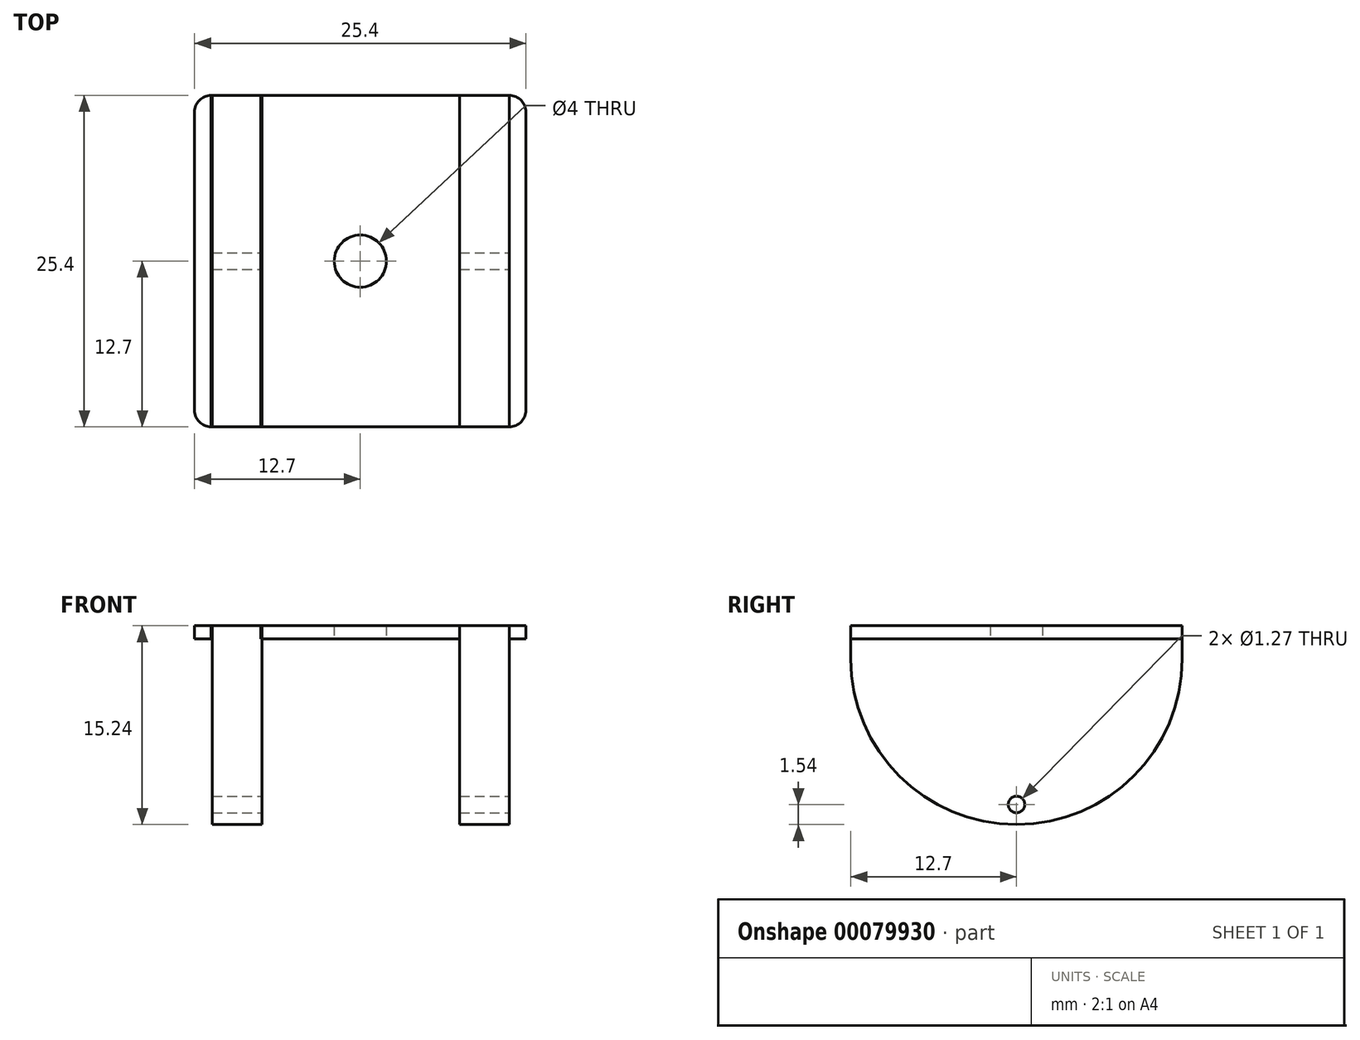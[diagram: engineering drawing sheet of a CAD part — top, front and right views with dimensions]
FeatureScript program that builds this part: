
annotation { "Feature Type Name" : "Feature", "Feature Type Description" : "" }
export const myFeature = defineFeature(function(context is Context, id is Id, definition is map)
    precondition{}
    {
        {
            var Q0;
            Q0=qCreatedBy(makeId("Top.planeOp"),FACE);
            var sketch = newSketch(context, id + "F0", { "sketchPlane" : qUnion([Q0])});
            skLineSegment(sketch, "E0.bottom", {"start": v(12.7, -12.7) * mm, "end": v(-12.7, -12.7) * mm});
            skLineSegment(sketch, "E0.top", {"start": v(12.7, 12.7) * mm, "end": v(-12.7, 12.7) * mm});
            skLineSegment(sketch, "E0.left", {"start": v(12.7, -12.7) * mm, "end": v(12.7, 12.7) * mm});
            skLineSegment(sketch, "E0.right", {"start": v(-12.7, -12.7) * mm, "end": v(-12.7, 12.7) * mm});
            skPoint(sketch, "E0.middle", {"position": v(0, 0) * mm});
            skLineSegment(sketch, "E1.bottom", {"start": v(-7.62, -12.7) * mm, "end": v(-11.43, -12.7) * mm});
            skLineSegment(sketch, "E1.top", {"start": v(-7.62, 12.7) * mm, "end": v(-11.43, 12.7) * mm});
            skLineSegment(sketch, "E1.left", {"start": v(-7.62, -12.7) * mm, "end": v(-7.62, 12.7) * mm});
            skLineSegment(sketch, "E1.right", {"start": v(-11.43, -12.7) * mm, "end": v(-11.43, 12.7) * mm});
            skPoint(sketch, "E1.middle", {"position": v(-9.53, 0) * mm});
            skPoint(sketch, "E1.middle.positionSnap0", {"position": v(-12.7, 0) * mm});
            skPoint(sketch, "E1.centerSnap0", {"position": v(-12.7, 0) * mm});
            skLineSegment(sketch, "E2", {"start": v(0, 12.7) * mm, "end": v(0, -12.7) * mm});
            skLineSegment(sketch, "E3.MirrorCS", {"start": v(11.43, -12.7) * mm, "end": v(11.43, 12.7) * mm});
            skLineSegment(sketch, "E4.MirrorCS", {"start": v(7.62, -12.7) * mm, "end": v(7.62, 12.7) * mm});
            skCircle(sketch, "E5", {"center": v(0, 0) * mm, "radius": 2 * mm});
            skSolve(sketch);
        }
        {
            var Q0;
            {var subQ0=sQuery(id+"F0.wireOp",EDGE,"E0.right");Q0=makeQuery(id+"F0.imprint","IMPRINT",FACE,{"disambiguationData":[TD([[makeQuery(id+"F0.imprint","IMPRINT",EDGE,{"derivedFrom":subQ0}),-1.0]])]});}
            var Q1;
            {var subQ0=sQuery(id+"F0.wireOp",EDGE,"E0.left");Q1=makeQuery(id+"F0.imprint","IMPRINT",FACE,{"disambiguationData":[TD([[makeQuery(id+"F0.imprint","IMPRINT",EDGE,{"derivedFrom":subQ0}),1.0]])]});}
            var Q2;
            {var subQ0=sQuery(id+"F0.wireOp",EDGE,"E2");Q2=makeQuery(id+"F0.imprint","IMPRINT",FACE,{"disambiguationData":[TD([[makeQuery(id+"F0.imprint","IMPRINT",EDGE,{"derivedFrom":subQ0}),1.0]])]});}
            var Q3;
            {var subQ0=sQuery(id+"F0.wireOp",EDGE,"E1.left");Q3=makeQuery(id+"F0.imprint","IMPRINT",FACE,{"disambiguationData":[TD([[makeQuery(id+"F0.imprint","IMPRINT",EDGE,{"derivedFrom":subQ0}),-1.0]])]});}
            extrude(context, id + "F1", {"entities" : qUnion([Q0, Q1, Q2, Q3]), "depth" : 1 * mm});
        }
        {
            var Q0;
            Q0=makeQuery(id+"F1.opExtrude","SWEPT_FACE",FACE,{"disambiguationData":[OSD([sQuery(id+"F0.wireOp",EDGE,"E3.MirrorCS")])]});
            var sketch = newSketch(context, id + "F2", { "sketchPlane" : qUnion([Q0])});
            skLineSegment(sketch, "E6.bottom", {"start": v(-12.7, 1) * mm, "end": v(12.7, 1) * mm});
            skLineSegment(sketch, "E6.top", {"start": v(-12.7, -14.24) * mm, "end": v(12.7, -14.24) * mm});
            skLineSegment(sketch, "E6.left", {"start": v(-12.7, 1) * mm, "end": v(-12.7, -14.24) * mm});
            skLineSegment(sketch, "E6.right", {"start": v(12.7, 1) * mm, "end": v(12.7, -14.24) * mm});
            skCircle(sketch, "E7", {"center": v(0, -12.7) * mm, "radius": 0.64 * mm});
            skSolve(sketch);
        }
        {
            var Q0;
            {var subQ0=sQuery(id+"F2.wireOp",EDGE,"E6.top");Q0=makeQuery(id+"F2.imprint","IMPRINT",FACE,{"disambiguationData":[TD([[makeQuery(id+"F2.imprint","IMPRINT",EDGE,{"derivedFrom":subQ0}),1.0]])]});}
            var Q1;
            {var subQ0=sQuery(id+"F2.wireOp",EDGE,"E6.bottom");Q1=makeQuery(id+"F2.imprint","IMPRINT",FACE,{"disambiguationData":[TD([[makeQuery(id+"F2.imprint","IMPRINT",EDGE,{"derivedFrom":subQ0}),1.0]])]});}
            extrude(context, id + "F3", {"entities" : qUnion([Q0, Q1]), "depth" : 3.8 * mm});
        }
        {
            var Q0;
            Q0=makeQuery(id+"F3.opExtrude","SWEPT_BODY",BODY,{"disambiguationData":[OSD([sQuery(id+"F2.wireOp",EDGE,"E6.bottom"),sQuery(id+"F2.wireOp",EDGE,"E6.top"),sQuery(id+"F2.wireOp",EDGE,"E6.left"),sQuery(id+"F2.wireOp",EDGE,"E6.right"),sQuery(id+"F2.wireOp",EDGE,"E7")])]});
            transform(context, id + "F4", {"entities" : qUnion([Q0]), "transformType" : TransformType.TRANSLATION_3D, "dx" : -18.96 * mm, "dy" : 0 * mm, "dz" : 0 * mm, "makeCopy" : true});
        }
        {
            var Q0;
            Q0=makeQuery(id+"F3.opExtrude","SWEPT_EDGE",EDGE,{"disambiguationData":[OSD([sQuery(id+"F2.wireOp",EDGE,"E6.top"),sQuery(id+"F2.wireOp",EDGE,"E6.right")])]});
            var Q1;
            Q1=makeQuery(id+"F3.opExtrude","SWEPT_EDGE",EDGE,{"disambiguationData":[OSD([sQuery(id+"F2.wireOp",EDGE,"E6.top"),sQuery(id+"F2.wireOp",EDGE,"E6.left")])]});
            fillet(context, id + "F5", {"entities" : qUnion([Q0, Q1]), "radius" : 12.7 * mm, "tangentPropagation" : true, "allowEdgeOverflow" : false});
        }
        {
            var Q0;
            Q0=makeQuery(id+"F4.opPattern","COPY",EDGE,{"derivedFrom":makeQuery(id+"F3.opExtrude","SWEPT_EDGE",EDGE,{"disambiguationData":[OSD([sQuery(id+"F2.wireOp",EDGE,"E6.top"),sQuery(id+"F2.wireOp",EDGE,"E6.right")])]}),"instanceName":"1"});
            var Q1;
            Q1=makeQuery(id+"F4.opPattern","COPY",EDGE,{"derivedFrom":makeQuery(id+"F3.opExtrude","SWEPT_EDGE",EDGE,{"disambiguationData":[OSD([sQuery(id+"F2.wireOp",EDGE,"E6.top"),sQuery(id+"F2.wireOp",EDGE,"E6.left")])]}),"instanceName":"1"});
            fillet(context, id + "F6", {"entities" : qUnion([Q0, Q1]), "radius" : 12.7 * mm, "tangentPropagation" : true, "allowEdgeOverflow" : false});
        }
        {
            var Q0;
            Q0=makeQuery(id+"F1.opExtrude","SWEPT_EDGE",EDGE,{"disambiguationData":[OSD([sQuery(id+"F0.wireOp",EDGE,"E0.bottom"),sQuery(id+"F0.wireOp",EDGE,"E0.right")])]});
            var Q1;
            Q1=makeQuery(id+"F1.opExtrude","SWEPT_EDGE",EDGE,{"disambiguationData":[OSD([sQuery(id+"F0.wireOp",EDGE,"E0.bottom"),sQuery(id+"F0.wireOp",EDGE,"E0.left")])]});
            var Q2;
            Q2=makeQuery(id+"F1.opExtrude","SWEPT_EDGE",EDGE,{"disambiguationData":[OSD([sQuery(id+"F0.wireOp",EDGE,"E0.top"),sQuery(id+"F0.wireOp",EDGE,"E0.left")])]});
            var Q3;
            Q3=makeQuery(id+"F1.opExtrude","SWEPT_EDGE",EDGE,{"disambiguationData":[OSD([sQuery(id+"F0.wireOp",EDGE,"E0.top"),sQuery(id+"F0.wireOp",EDGE,"E0.right")])]});
            fillet(context, id + "F7", {"entities" : qUnion([Q0, Q1, Q2, Q3]), "radius" : 1.27 * mm, "tangentPropagation" : true, "allowEdgeOverflow" : false});
        }
        {
            var Q0;
            Q0=makeQuery(id+"F1.opExtrude","SWEPT_FACE",FACE,{"disambiguationData":[OSD([sQuery(id+"F0.wireOp",EDGE,"E1.right")])]});
            extrude(context, id + "F8", {"entities" : qUnion([Q0]), "depth" : 0.09 * mm});
        }
    });
